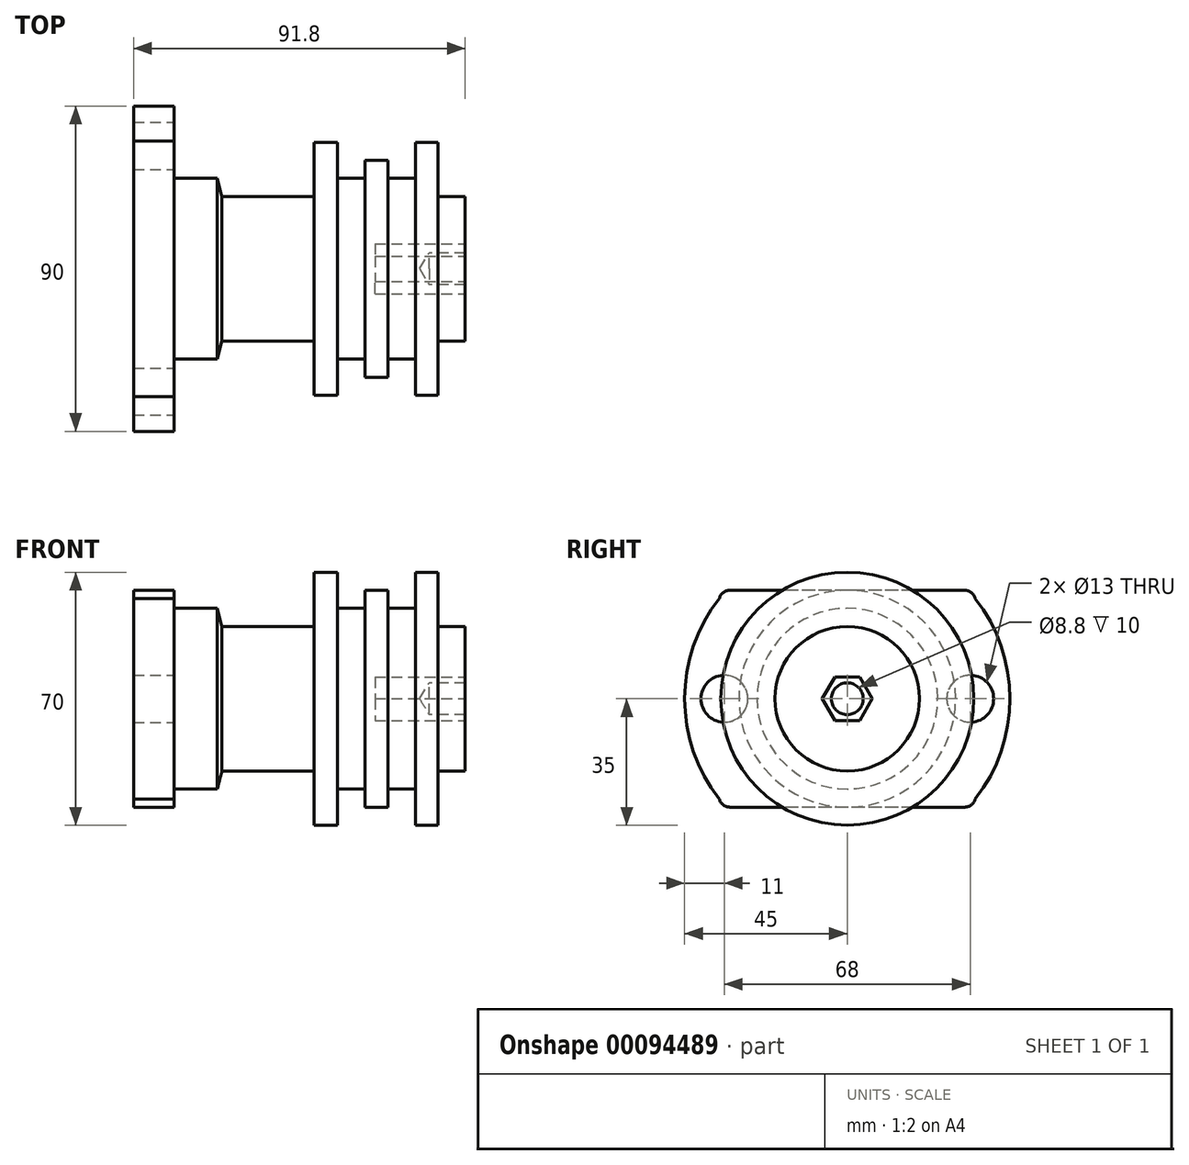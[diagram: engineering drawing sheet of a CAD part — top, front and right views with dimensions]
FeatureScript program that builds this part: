
annotation { "Feature Type Name" : "Feature", "Feature Type Description" : "" }
export const myFeature = defineFeature(function(context is Context, id is Id, definition is map)
    precondition{}
    {
        {
            var Q0;
            Q0=qCreatedBy(makeId("Top.planeOp"),FACE);
            var sketch = newSketch(context, id + "F0", { "sketchPlane" : qUnion([Q0])});
            skLineSegment(sketch, "E0", {"start": v(11.2, -25) * mm, "end": v(23.2, -25) * mm});
            skLineSegment(sketch, "E1", {"start": v(23.2, -25) * mm, "end": v(24.5, -20) * mm});
            skLineSegment(sketch, "E2", {"start": v(24.5, -20) * mm, "end": v(50, -20) * mm});
            skLineSegment(sketch, "E3", {"start": v(50, -20) * mm, "end": v(50, -35) * mm});
            skLineSegment(sketch, "E4", {"start": v(50, -35) * mm, "end": v(56.5, -35) * mm});
            skLineSegment(sketch, "E5", {"start": v(56.5, -35) * mm, "end": v(56.5, -25) * mm});
            skLineSegment(sketch, "E6", {"start": v(56.5, -25) * mm, "end": v(64.1, -25) * mm});
            skLineSegment(sketch, "E7", {"start": v(64.1, -25) * mm, "end": v(64.1, -30) * mm});
            skLineSegment(sketch, "E8", {"start": v(64.1, -30) * mm, "end": v(70.4, -30) * mm});
            skLineSegment(sketch, "E9", {"start": v(70.4, -30) * mm, "end": v(70.4, -25) * mm});
            skLineSegment(sketch, "E10", {"start": v(70.4, -25) * mm, "end": v(78, -25) * mm});
            skLineSegment(sketch, "E11", {"start": v(78, -25) * mm, "end": v(78, -35) * mm});
            skLineSegment(sketch, "E12", {"start": v(78, -35) * mm, "end": v(84.3, -35) * mm});
            skLineSegment(sketch, "E13", {"start": v(84.3, -35) * mm, "end": v(84.3, -20) * mm});
            skLineSegment(sketch, "E14", {"start": v(84.3, -20) * mm, "end": v(91.8, -20) * mm});
            skLineSegment(sketch, "E15", {"start": v(0, 0) * mm, "end": v(91.8, 0) * mm});
            skLineSegment(sketch, "E16", {"start": v(91.8, -20) * mm, "end": v(91.8, 0) * mm});
            skLineSegment(sketch, "E17", {"start": v(115.09, 0) * mm, "end": v(-22.9, 0) * mm, "construction": true});
            skLineSegment(sketch, "E18", {"start": v(11.2, -25) * mm, "end": v(11.2, 0) * mm});
            skSolve(sketch);
        }
        {
            var Q0;
            Q0=makeQuery(id+"F0.imprint","IMPRINT",FACE,{"disambiguationData":[TD([[makeQuery(id+"F0.imprint","IMPRINT",EDGE,{"derivedFrom":sQuery(id+"F0.wireOp",EDGE,"E0")}),1.0]])]});
            var Q1;
            Q1=sQuery(id+"F0.wireOp",EDGE,"E17");
            revolve(context, id + "F1", {"entities" : qUnion([Q0]), "axis" : qUnion([Q1]), "revolveType" : RevolveType.FULL});
        }
        {
            var Q0;
            Q0=makeQuery(id+"F1.opRevolve","SWEPT_FACE",FACE,{"disambiguationData":[OSD([sQuery(id+"F0.wireOp",EDGE,"E18")])]});
            var sketch = newSketch(context, id + "F2", { "sketchPlane" : qUnion([Q0])});
            skLineSegment(sketch, "E19", {"start": v(0, 79.48) * mm, "end": v(0, -77.62) * mm, "construction": true});
            skLineSegment(sketch, "E20", {"start": v(0, 30) * mm, "end": v(32.5, 30) * mm});
            skArc(sketch, "E21", {"start": v(35.4, 27.79) * mm, "mid": v(34.32, 29.38) * mm, "end": v(32.5, 30) * mm});
            skArc(sketch, "E22", {"start": v(35.4, -27.79) * mm, "mid": v(45, 0) * mm, "end": v(35.4, 27.79) * mm});
            skArc(sketch, "E23", {"start": v(32.5, -30) * mm, "mid": v(34.32, -29.38) * mm, "end": v(35.4, -27.79) * mm});
            skLineSegment(sketch, "E24", {"start": v(32.5, -30) * mm, "end": v(0, -30) * mm});
            skLineSegment(sketch, "E25", {"start": v(126.12, 0) * mm, "end": v(282.45, 0) * mm, "construction": true});
            skLineSegment(sketch, "E26", {"start": v(207.65, 0) * mm, "end": v(207.65, 30) * mm, "construction": true});
            skLineSegment(sketch, "E27", {"start": v(207.65, 0) * mm, "end": v(207.65, -30) * mm, "construction": true});
            skLineSegment(sketch, "E28.MirrorCS", {"start": v(0, 30) * mm, "end": v(-32.5, 30) * mm});
            skArc(sketch, "E29.MirrorCS", {"start": v(-35.4, 27.79) * mm, "mid": v(-34.32, 29.38) * mm, "end": v(-32.5, 30) * mm});
            skArc(sketch, "E30.MirrorCS", {"start": v(-35.4, -27.79) * mm, "mid": v(-45, 0) * mm, "end": v(-35.4, 27.79) * mm});
            skArc(sketch, "E31.MirrorCS", {"start": v(-32.5, -30) * mm, "mid": v(-34.32, -29.38) * mm, "end": v(-35.4, -27.79) * mm});
            skLineSegment(sketch, "E32.MirrorCS", {"start": v(-32.5, -30) * mm, "end": v(0, -30) * mm});
            skCircle(sketch, "E33", {"center": v(34, 0) * mm, "radius": 6.5 * mm});
            skCircle(sketch, "E34.MirrorC", {"center": v(-34, 0) * mm, "radius": 6.5 * mm});
            skSolve(sketch);
        }
        {
            var Q0;
            Q0=makeQuery(id+"F2.imprint","IMPRINT",FACE,{"disambiguationData":[TD([[makeQuery(id+"F2.imprint","IMPRINT",EDGE,{"derivedFrom":sQuery(id+"F2.wireOp",EDGE,"E20")}),-1.0]])]});
            var Q1;
            Q1=makeQuery(id+"F2.imprint","IMPRINT",FACE,{"disambiguationData":[TD([[makeQuery(id+"F2.imprint","IMPRINT",EDGE,{"derivedFrom":makeQuery(id+"F1.opRevolve","SWEPT_EDGE",EDGE,{"disambiguationData":[OSD([sQuery(id+"F0.wireOp",EDGE,"E0"),sQuery(id+"F0.wireOp",EDGE,"E18")])]})}),-1.0]])]});
            extrude(context, id + "F3", {"entities" : qUnion([Q0, Q1]), "operationType" : NewBodyOperationType.ADD, "depth" : 11.2 * mm});
        }
        {
            var Q0;
            Q0=makeQuery(id+"F1.opRevolve","SWEPT_FACE",FACE,{"disambiguationData":[OSD([sQuery(id+"F0.wireOp",EDGE,"E16")])]});
            var sketch = newSketch(context, id + "F4", { "sketchPlane" : qUnion([Q0])});
            skCircle(sketch, "E35.cCircle", {"center": v(0, 0) * mm, "radius": 6 * mm, "construction": true});
            skLineSegment(sketch, "E35.0", {"start": v(3.46, -6) * mm, "end": v(-3.46, -6) * mm});
            skLineSegment(sketch, "E35.1", {"start": v(-3.46, -6) * mm, "end": v(-6.93, 0) * mm});
            skLineSegment(sketch, "E35.2", {"start": v(-6.93, 0) * mm, "end": v(-3.46, 6) * mm});
            skLineSegment(sketch, "E35.3", {"start": v(-3.46, 6) * mm, "end": v(3.46, 6) * mm});
            skLineSegment(sketch, "E35.4", {"start": v(3.46, 6) * mm, "end": v(6.93, 0) * mm});
            skLineSegment(sketch, "E35.5", {"start": v(6.93, 0) * mm, "end": v(3.46, -6) * mm});
            skPoint(sketch, "E35.0.midPoint", {"position": v(0, -6) * mm});
            skLineSegment(sketch, "E36", {"start": v(0, -8.76) * mm, "end": v(0, 9.39) * mm, "construction": true});
            skLineSegment(sketch, "E37", {"start": v(10.27, 0) * mm, "end": v(-10.37, 0) * mm, "construction": true});
            skSolve(sketch);
        }
        {
            var Q0;
            Q0=makeQuery(id+"F4.imprint","IMPRINT",FACE,{"disambiguationData":[TD([[makeQuery(id+"F4.imprint","IMPRINT",EDGE,{"derivedFrom":sQuery(id+"F4.wireOp",EDGE,"E35.0")}),-1.0]])]});
            extrude(context, id + "F5", {"entities" : qUnion([Q0]), "oppositeDirection" : true, "depth" : 25 * mm});
        }
        {
            var Q0;
            Q0=makeQuery(id+"F5.opExtrude","SWEPT_BODY",BODY,{"disambiguationData":[OSD([sQuery(id+"F4.wireOp",EDGE,"E35.0"),sQuery(id+"F4.wireOp",EDGE,"E35.1"),sQuery(id+"F4.wireOp",EDGE,"E35.2"),sQuery(id+"F4.wireOp",EDGE,"E35.3"),sQuery(id+"F4.wireOp",EDGE,"E35.4"),sQuery(id+"F4.wireOp",EDGE,"E35.5")])]});
            var Q1;
            Q1=makeQuery(id+"F1.opRevolve","SWEPT_BODY",BODY,{"disambiguationData":[OSD([sQuery(id+"F0.wireOp",EDGE,"E0"),sQuery(id+"F0.wireOp",EDGE,"E1"),sQuery(id+"F0.wireOp",EDGE,"E2"),sQuery(id+"F0.wireOp",EDGE,"E3"),sQuery(id+"F0.wireOp",EDGE,"E4"),sQuery(id+"F0.wireOp",EDGE,"E5"),sQuery(id+"F0.wireOp",EDGE,"E6"),sQuery(id+"F0.wireOp",EDGE,"E7"),sQuery(id+"F0.wireOp",EDGE,"E8"),sQuery(id+"F0.wireOp",EDGE,"E9"),sQuery(id+"F0.wireOp",EDGE,"E10"),sQuery(id+"F0.wireOp",EDGE,"E11"),sQuery(id+"F0.wireOp",EDGE,"E12"),sQuery(id+"F0.wireOp",EDGE,"E13"),sQuery(id+"F0.wireOp",EDGE,"E14"),sQuery(id+"F0.wireOp",EDGE,"E15"),sQuery(id+"F0.wireOp",EDGE,"E16"),sQuery(id+"F0.wireOp",EDGE,"E18")])]});
            booleanBodies(context, id + "F6", {"operationType" : BooleanOperationType.SUBTRACTION, "tools" : qUnion([Q0]), "targets" : qUnion([Q1]), "keepTools" : true});
        }
        {
            var Q0;
            Q0=sQuery(id+"F4.wireOp",VERTEX,"E35.cCircle.center");
            var Q1;
            Q1=makeQuery(id+"F5.opExtrude","SWEPT_BODY",BODY,{"disambiguationData":[OSD([sQuery(id+"F4.wireOp",EDGE,"E35.0"),sQuery(id+"F4.wireOp",EDGE,"E35.1"),sQuery(id+"F4.wireOp",EDGE,"E35.2"),sQuery(id+"F4.wireOp",EDGE,"E35.3"),sQuery(id+"F4.wireOp",EDGE,"E35.4"),sQuery(id+"F4.wireOp",EDGE,"E35.5")])]});
            hole(context, id + "F7", {"style" : HoleStyle.SIMPLE, "endStyle" : HoleEndStyle.BLIND, "standardTappedOrClearance" : lookupTablePath({ "standard" : "ISO", "fit" : "Normal", "size" : "M8", "type" : "Clearance" }), "standardBlindInLast" : lookupTablePath({ "fit" : "Standard", "standard" : "ISO", "size" : "M8", "type" : "Clearance" }), "holeDiameter" : 8.8 * mm, "holeDepth" : 10 * mm, "locations" : qUnion([Q0]), "scope" : qUnion([Q1]), "startStyle" : HoleStartStyle.PART});
        }
    });
